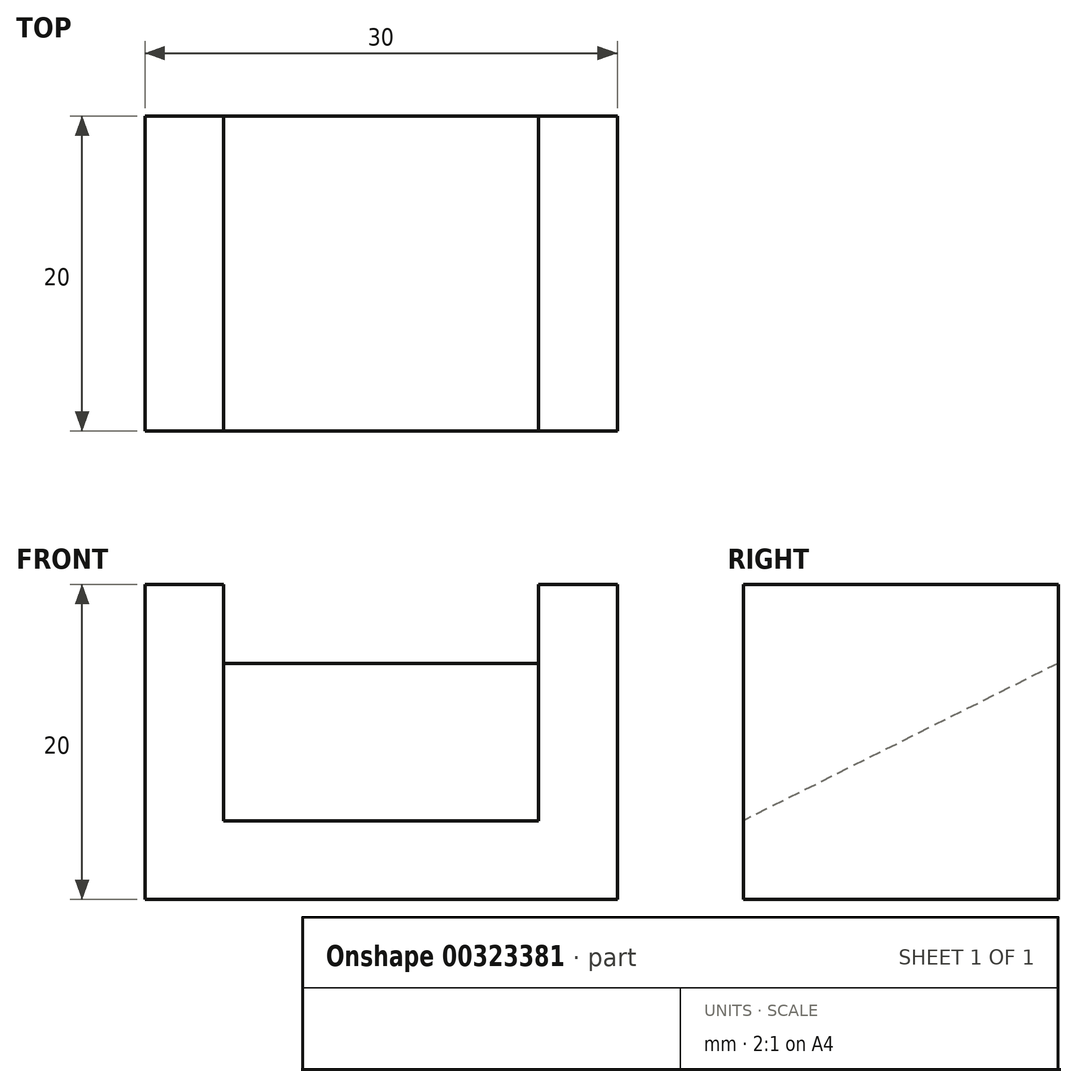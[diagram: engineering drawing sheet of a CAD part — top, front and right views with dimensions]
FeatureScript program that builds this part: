
annotation { "Feature Type Name" : "Feature", "Feature Type Description" : "" }
export const myFeature = defineFeature(function(context is Context, id is Id, definition is map)
    precondition{}
    {
        {
            var Q0;
            Q0=qCreatedBy(makeId("Front.planeOp"),FACE);
            var sketch = newSketch(context, id + "F0", { "sketchPlane" : qUnion([Q0])});
            skLineSegment(sketch, "E0", {"start": v(-15, 15) * mm, "end": v(-15, -5) * mm});
            skLineSegment(sketch, "E1", {"start": v(-15, -5) * mm, "end": v(15, -5) * mm});
            skLineSegment(sketch, "E2", {"start": v(15, -5) * mm, "end": v(15, 15) * mm});
            skLineSegment(sketch, "E3", {"start": v(15, 15) * mm, "end": v(10, 15) * mm});
            skLineSegment(sketch, "E4", {"start": v(10, 15) * mm, "end": v(10, 0) * mm});
            skLineSegment(sketch, "E5", {"start": v(10, 0) * mm, "end": v(-10, 0) * mm});
            skLineSegment(sketch, "E6", {"start": v(-10, 0) * mm, "end": v(-10, 15) * mm});
            skLineSegment(sketch, "E7", {"start": v(-10, 15) * mm, "end": v(-15, 15) * mm});
            skSolve(sketch);
        }
        {
            var Q0;
            Q0=makeQuery(id+"F0.imprint","IMPRINT",FACE,{"disambiguationData":[TD([[makeQuery(id+"F0.imprint","IMPRINT",EDGE,{"derivedFrom":sQuery(id+"F0.wireOp",EDGE,"E0")}),1.0]])]});
            extrude(context, id + "F1", {"entities" : qUnion([Q0]), "depth" : 20 * mm});
        }
        {
            var Q0;
            Q0=makeQuery(id+"F1.opExtrude","SWEPT_FACE",FACE,{"disambiguationData":[OSD([sQuery(id+"F0.wireOp",EDGE,"E6")])]});
            var sketch = newSketch(context, id + "F2", { "sketchPlane" : qUnion([Q0])});
            skLineSegment(sketch, "E8", {"start": v(-20, 0) * mm, "end": v(0, 10) * mm});
            skLineSegment(sketch, "E9", {"start": v(0, 10) * mm, "end": v(0, 0) * mm});
            skLineSegment(sketch, "E10", {"start": v(0, 0) * mm, "end": v(-20, 0) * mm});
            skSolve(sketch);
        }
        {
            var Q0;
            Q0 = qSketchRegion(id + "F2", true);
            extrude(context, id + "F3", {"entities" : qUnion([Q0]), "operationType" : NewBodyOperationType.ADD, "depth" : 20.3 * mm});
        }
    });
